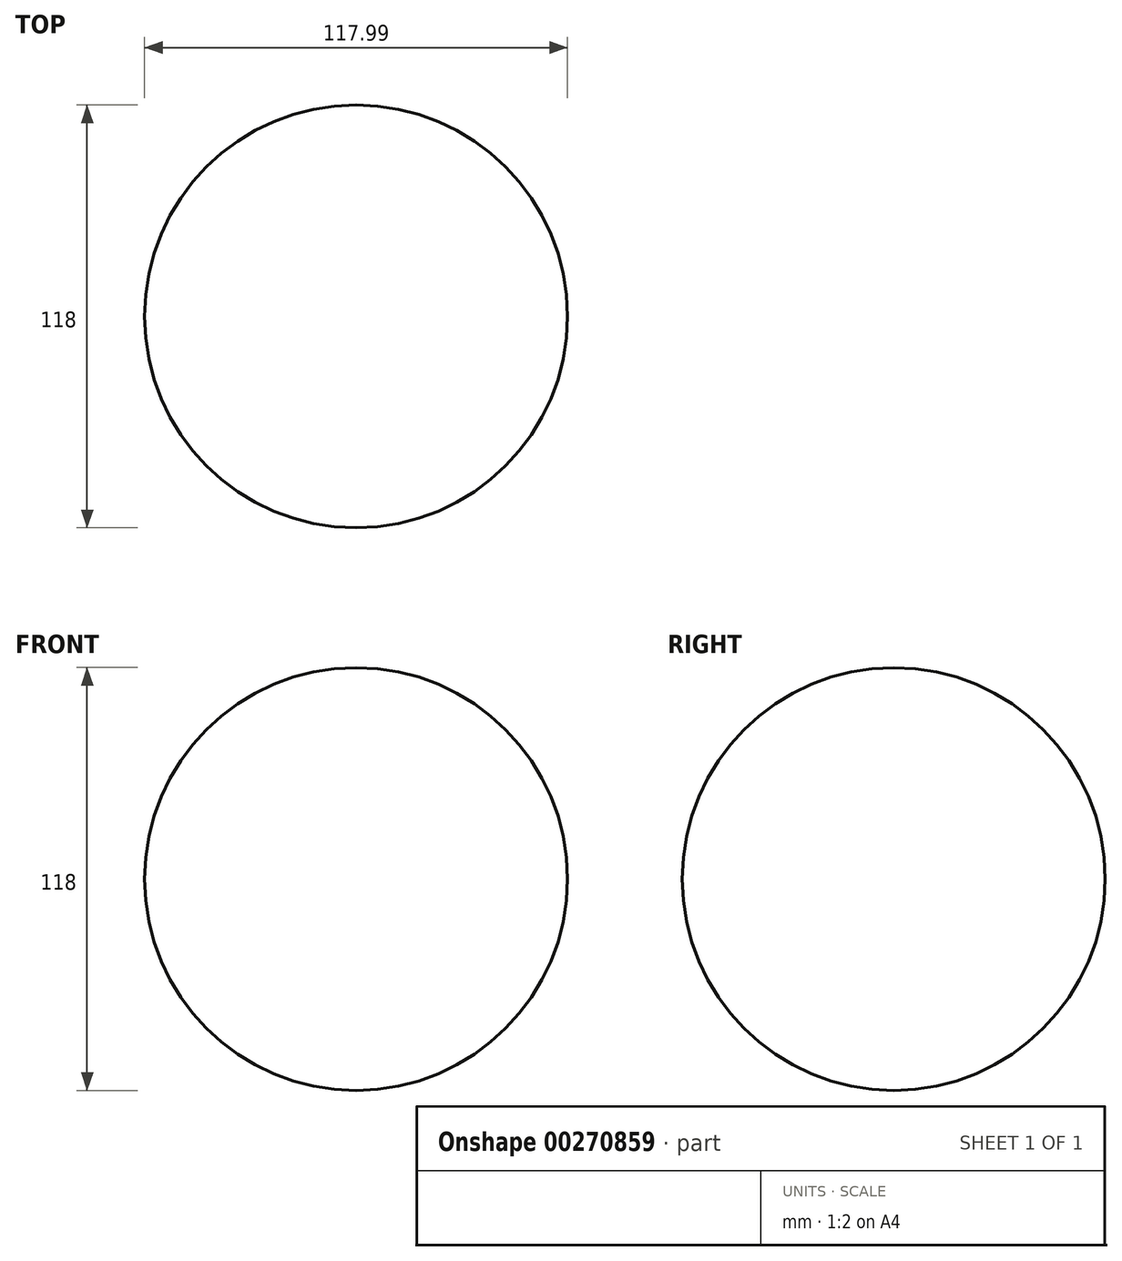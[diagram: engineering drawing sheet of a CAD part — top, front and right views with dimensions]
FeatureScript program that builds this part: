
annotation { "Feature Type Name" : "Feature", "Feature Type Description" : "" }
export const myFeature = defineFeature(function(context is Context, id is Id, definition is map)
    precondition{}
    {
        {
            var Q0;
            Q0=qCreatedBy(makeId("Front.planeOp"),FACE);
            var sketch = newSketch(context, id + "F0", { "sketchPlane" : qUnion([Q0])});
            skArc(sketch, "E0", {"start": v(-56.52, 113.04) * mm, "mid": v(-115.52, 54.04) * mm, "end": v(-56.52, -4.96) * mm});
            skLineSegment(sketch, "E1", {"start": v(-56.52, 54.04) * mm, "end": v(-56.52, 113.04) * mm});
            skLineSegment(sketch, "E2", {"start": v(-56.52, 54.04) * mm, "end": v(-56.52, -4.96) * mm});
            skSolve(sketch);
        }
        {
            var Q0;
            Q0 = qSketchRegion(id + "F0", true);
            var Q1;
            Q1=sQuery(id+"F0.wireOp",EDGE,"E1");
            revolve(context, id + "F1", {"entities" : qUnion([Q0]), "axis" : qUnion([Q1]), "revolveType" : RevolveType.FULL});
        }
    });
